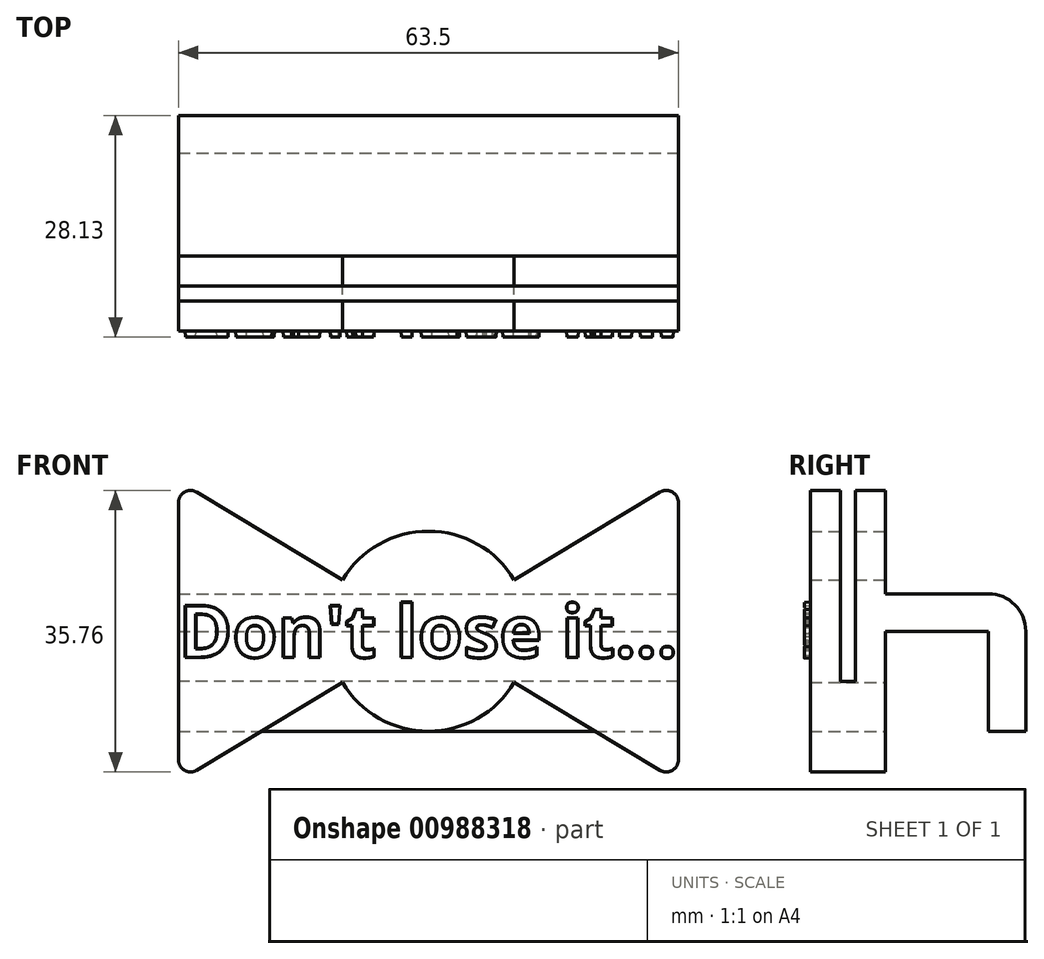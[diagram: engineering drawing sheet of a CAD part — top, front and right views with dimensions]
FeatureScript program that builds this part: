
annotation { "Feature Type Name" : "Feature", "Feature Type Description" : "" }
export const myFeature = defineFeature(function(context is Context, id is Id, definition is map)
    precondition{}
    {
        {
            var Q0;
            Q0=qCreatedBy(makeId("Front.planeOp"),FACE);
            var sketch = newSketch(context, id + "F0", { "sketchPlane" : qUnion([Q0])});
            skArc(sketch, "E0", {"start": v(-10.9, -6.53) * mm, "mid": v(0, -12.7) * mm, "end": v(10.9, -6.53) * mm});
            skLineSegment(sketch, "E1", {"start": v(-29.44, 17.67) * mm, "end": v(-10.9, 6.53) * mm});
            skLineSegment(sketch, "E2", {"start": v(31.75, -16.36) * mm, "end": v(31.75, 16.36) * mm});
            skLineSegment(sketch, "E3", {"start": v(29.44, 17.67) * mm, "end": v(10.9, 6.53) * mm});
            skLineSegment(sketch, "E4", {"start": v(-31.75, -16.36) * mm, "end": v(-31.75, 16.36) * mm});
            skLineSegment(sketch, "E5.trimOffspring", {"start": v(10.9, -6.53) * mm, "end": v(29.44, -17.67) * mm});
            skLineSegment(sketch, "E6.trimOffspring", {"start": v(-10.9, -6.53) * mm, "end": v(-29.44, -17.67) * mm});
            skArc(sketch, "E7.trimOffspring", {"start": v(10.9, 6.53) * mm, "mid": v(0, 12.7) * mm, "end": v(-10.9, 6.53) * mm});
            skPoint(sketch, "E8.visualSharp", {"position": v(-31.75, 19.05) * mm});
            skArc(sketch, "E8.filletArc", {"start": v(-29.44, 17.67) * mm, "mid": v(-30.98, 17.68) * mm, "end": v(-31.75, 16.36) * mm});
            skPoint(sketch, "E9.visualSharp", {"position": v(-31.75, -19.05) * mm});
            skArc(sketch, "E9.filletArc", {"start": v(-31.75, -16.36) * mm, "mid": v(-30.98, -17.68) * mm, "end": v(-29.44, -17.67) * mm});
            skPoint(sketch, "E10.visualSharp", {"position": v(31.75, -19.05) * mm});
            skArc(sketch, "E10.filletArc", {"start": v(29.44, -17.67) * mm, "mid": v(30.98, -17.68) * mm, "end": v(31.75, -16.36) * mm});
            skPoint(sketch, "E11.visualSharp", {"position": v(31.75, 19.05) * mm});
            skArc(sketch, "E11.filletArc", {"start": v(31.75, 16.36) * mm, "mid": v(30.98, 17.68) * mm, "end": v(29.44, 17.67) * mm});
            skSolve(sketch);
        }
        {
            var Q0;
            Q0=makeQuery(id+"F0.imprint","IMPRINT",FACE,{"disambiguationData":[TD([[makeQuery(id+"F0.imprint","IMPRINT",EDGE,{"derivedFrom":sQuery(id+"F0.wireOp",EDGE,"E0")}),1.0]])]});
            extrude(context, id + "F1", {"entities" : qUnion([Q0]), "depth" : 9.52 * mm, "offsetDistance" : 25.4 * mm});
        }
        {
            var Q0;
            Q0=qCreatedBy(makeId("Top.planeOp"),FACE);
            var sketch = newSketch(context, id + "F2", { "sketchPlane" : qUnion([Q0])});
            skLineSegment(sketch, "E12", {"start": v(0, 0) * mm, "end": v(0, -9.53) * mm, "construction": true});
            skLineSegment(sketch, "E13.bottom", {"start": v(31.75, -3.81) * mm, "end": v(-31.75, -3.81) * mm});
            skLineSegment(sketch, "E13.top", {"start": v(31.75, -5.72) * mm, "end": v(-31.75, -5.72) * mm});
            skLineSegment(sketch, "E13.left", {"start": v(31.75, -3.81) * mm, "end": v(31.75, -5.72) * mm});
            skLineSegment(sketch, "E13.right", {"start": v(-31.75, -3.81) * mm, "end": v(-31.75, -5.72) * mm});
            skPoint(sketch, "E13.middle", {"position": v(0, -4.76) * mm});
            skSolve(sketch);
        }
        {
            var Q0;
            Q0 = qSketchRegion(id + "F2", true);
            extrude(context, id + "F3", {"entities" : qUnion([Q0]), "operationType" : NewBodyOperationType.REMOVE, "depth" : 25.4 * mm, "offsetDistance" : 25.4 * mm});
        }
        {
            var Q0;
            Q0=makeQuery(id+"F3.boolean.opBoolean","COPY",FACE,{"derivedFrom":makeQuery(id+"F3.opExtrude","CAP_FACE",FACE,{"disambiguationData":[OSD([sQuery(id+"F2.wireOp",EDGE,"E13.bottom"),sQuery(id+"F2.wireOp",EDGE,"E13.top"),sQuery(id+"F2.wireOp",EDGE,"E13.left"),sQuery(id+"F2.wireOp",EDGE,"E13.right")])],"isStart":true})});
            extrude(context, id + "F4", {"entities" : qUnion([Q0]), "operationType" : NewBodyOperationType.REMOVE, "oppositeDirection" : true, "depth" : 6.35 * mm, "offsetDistance" : 25.4 * mm});
        }
        {
            var Q0;
            Q0=makeQuery(id+"F1.opExtrude","SWEPT_FACE",FACE,{"disambiguationData":[OSD([sQuery(id+"F0.wireOp",EDGE,"E2")])]});
            var sketch = newSketch(context, id + "F5", { "sketchPlane" : qUnion([Q0])});
            skLineSegment(sketch, "E14", {"start": v(0, 4.76) * mm, "end": v(13.08, 4.76) * mm});
            skLineSegment(sketch, "E15", {"start": v(17.84, 0) * mm, "end": v(17.84, -12.7) * mm});
            skLineSegment(sketch, "E16", {"start": v(17.84, -12.7) * mm, "end": v(13.08, -12.7) * mm});
            skLineSegment(sketch, "E17", {"start": v(13.08, -12.7) * mm, "end": v(13.08, 0) * mm});
            skLineSegment(sketch, "E18", {"start": v(13.08, 0) * mm, "end": v(0, 0) * mm});
            skLineSegment(sketch, "E19", {"start": v(0, 0) * mm, "end": v(0, 4.76) * mm});
            skPoint(sketch, "E20.visualSharp", {"position": v(17.84, 4.76) * mm});
            skArc(sketch, "E20.filletArc", {"start": v(17.84, 0) * mm, "mid": v(16.45, 3.37) * mm, "end": v(13.08, 4.76) * mm});
            skSolve(sketch);
        }
        {
            var Q0;
            Q0=makeQuery(id+"F5.imprint","IMPRINT",FACE,{"disambiguationData":[TD([[makeQuery(id+"F5.imprint","IMPRINT",EDGE,{"derivedFrom":sQuery(id+"F5.wireOp",EDGE,"E14")}),-1.0]])]});
            var Q1;
            Q1=makeQuery(id+"F1.opExtrude","SWEPT_FACE",FACE,{"disambiguationData":[OSD([sQuery(id+"F0.wireOp",EDGE,"E4")])]});
            extrude(context, id + "F6", {"entities" : qUnion([Q0]), "operationType" : NewBodyOperationType.ADD, "endBound" : BoundingType.UP_TO_SURFACE, "oppositeDirection" : true, "depth" : 25.4 * mm, "endBoundEntityFace" : qUnion([Q1]), "offsetDistance" : 25.4 * mm});
        }
        {
            var Q0;
            Q0=makeQuery(id+"F1.opExtrude","CAP_FACE",FACE,{"disambiguationData":[OSD([sQuery(id+"F0.wireOp",EDGE,"E0"),sQuery(id+"F0.wireOp",EDGE,"E1"),sQuery(id+"F0.wireOp",EDGE,"E2"),sQuery(id+"F0.wireOp",EDGE,"E3"),sQuery(id+"F0.wireOp",EDGE,"E4"),sQuery(id+"F0.wireOp",EDGE,"E5.trimOffspring"),sQuery(id+"F0.wireOp",EDGE,"E6.trimOffspring"),sQuery(id+"F0.wireOp",EDGE,"E7.trimOffspring"),sQuery(id+"F0.wireOp",EDGE,"E8.filletArc"),sQuery(id+"F0.wireOp",EDGE,"E9.filletArc"),sQuery(id+"F0.wireOp",EDGE,"E10.filletArc"),sQuery(id+"F0.wireOp",EDGE,"E11.filletArc")])],"isStart":false});
            var sketch = newSketch(context, id + "F7", { "sketchPlane" : qUnion([Q0])});
            skText(sketch, "E21", { "text": "Don\'t lose it...", "fontName": "OpenSans-Bold.ttf"});
            skLineSegment(sketch, "E22", {"start": v(31.75, 0) * mm, "end": v(-31.75, 0) * mm, "construction": true});
            const initialGuessF7  = {"E21": [-0.03175, -0.00334, 1, 0, 0.00667]};
            skSetInitialGuess(sketch, initialGuessF7);
            skSolve(sketch);
        }
        {
            var Q0;
            Q0 = qSketchRegion(id + "F7", true);
            var Q1;
            {var subQ0=sQuery(id+"F2.wireOp",EDGE,"E13.top");Q1=makeQuery(id+"F4.boolean.opBoolean","MERGE",FACE,{"derivedFrom":[makeQuery(id+"F3.boolean.opBoolean","COPY",FACE,{"derivedFrom":makeQuery(id+"F3.opExtrude","SWEPT_FACE",FACE,{"disambiguationData":[OSD([subQ0])]})})],"fromTools":[makeQuery(id+"F4.opExtrude","SWEPT_FACE",FACE,{"disambiguationData":[OSD([subQ0])]})]});}
            extrude(context, id + "F8", {"entities" : qUnion([Q0]), "operationType" : NewBodyOperationType.ADD, "depth" : 0.76 * mm, "endBoundEntityFace" : qUnion([Q1]), "offsetDistance" : 25.4 * mm, "hasDraft" : true, "draftAngle" : 3 * degree, "draftPullDirection" : true});
        }
    });
